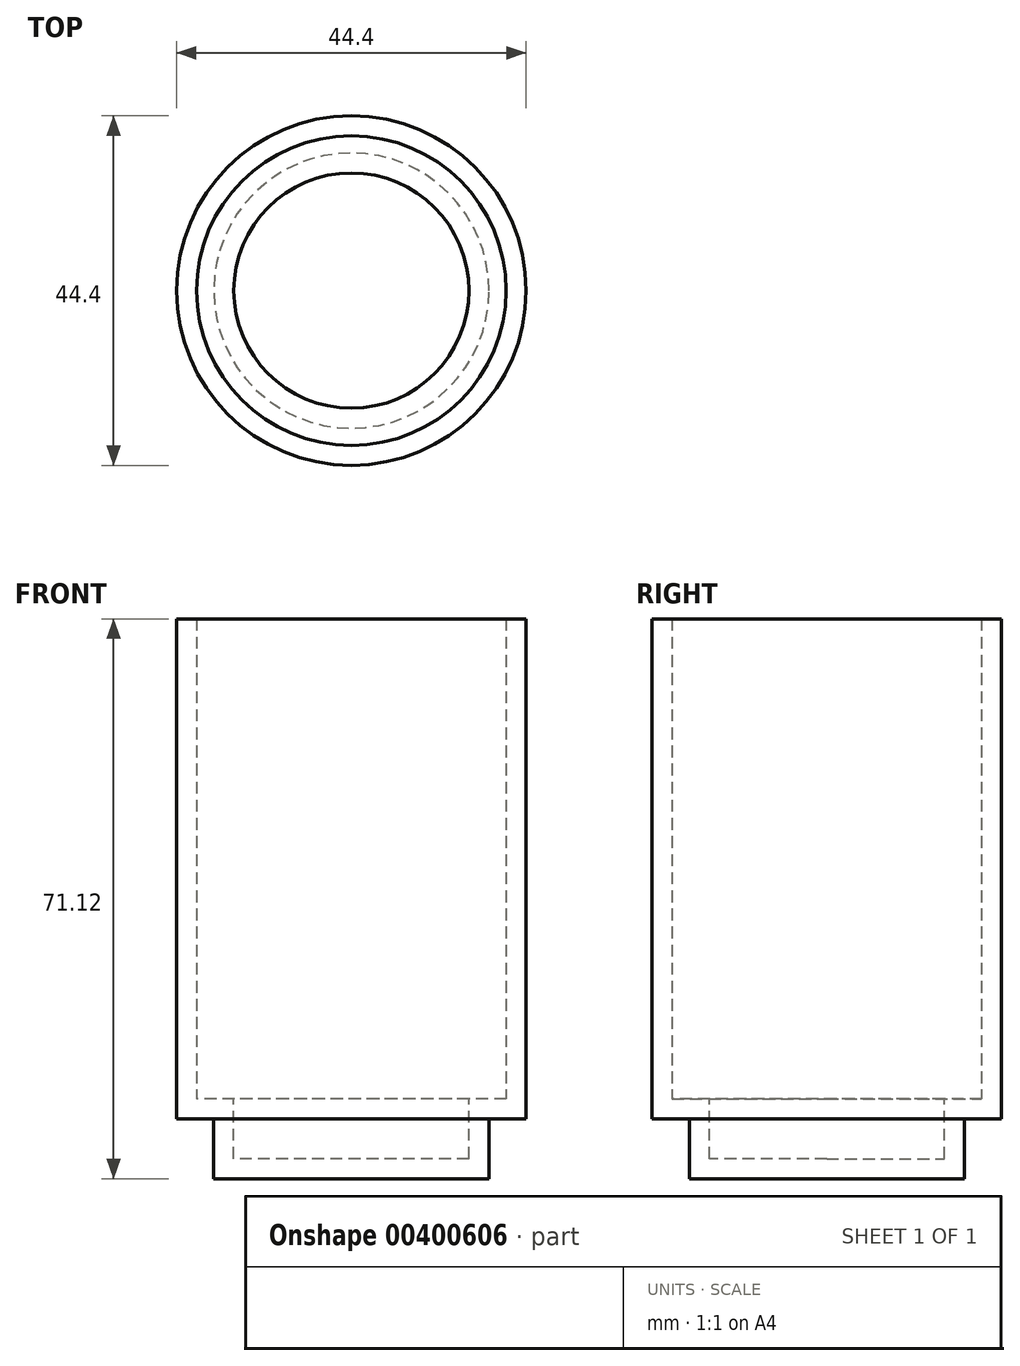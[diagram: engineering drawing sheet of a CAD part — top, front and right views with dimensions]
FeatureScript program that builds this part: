
annotation { "Feature Type Name" : "Feature", "Feature Type Description" : "" }
export const myFeature = defineFeature(function(context is Context, id is Id, definition is map)
    precondition{}
    {
        {
            var Q0;
            Q0=qCreatedBy(makeId("Top.planeOp"),FACE);
            var sketch = newSketch(context, id + "F0", { "sketchPlane" : qUnion([Q0])});
            skCircle(sketch, "E0", {"center": v(-14.82, 37.27) * mm, "radius": 22.2 * mm});
            skSolve(sketch);
        }
        {
            var Q0;
            Q0 = qSketchRegion(id + "F0", true);
            extrude(context, id + "F1", {"entities" : qUnion([Q0]), "depth" : 63.5 * mm});
        }
        {
            var Q0;
            Q0=makeQuery(id+"F1.opExtrude","CAP_FACE",FACE,{"disambiguationData":[OSD([sQuery(id+"F0.wireOp",EDGE,"E0")])],"isStart":true});
            var sketch = newSketch(context, id + "F2", { "sketchPlane" : qUnion([Q0])});
            skPoint(sketch, "E1", {"position": v(-14.82, -37.27) * mm});
            skCircle(sketch, "E2", {"center": v(-14.82, -37.27) * mm, "radius": 17.48 * mm});
            skSolve(sketch);
        }
        {
            var Q0;
            Q0=makeQuery(id+"F2.imprint","IMPRINT",FACE,{"disambiguationData":[TD([[makeQuery(id+"F2.imprint","IMPRINT",EDGE,{"derivedFrom":sQuery(id+"F2.wireOp",EDGE,"E2")}),1.0]])]});
            extrude(context, id + "F3", {"entities" : qUnion([Q0]), "operationType" : NewBodyOperationType.ADD, "depth" : 7.62 * mm});
        }
        {
            var Q0;
            Q0=makeQuery(id+"F1.opExtrude","CAP_FACE",FACE,{"disambiguationData":[OSD([sQuery(id+"F0.wireOp",EDGE,"E0")])],"isStart":false});
            shell(context, id + "F4", {"entities" : qUnion([Q0]), "thickness" : 2.54 * mm});
        }
    });
